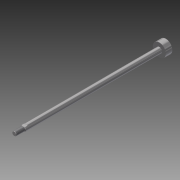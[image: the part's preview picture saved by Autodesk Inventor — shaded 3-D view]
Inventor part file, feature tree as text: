
AUTODESK INVENTOR PART (.ipt)
format: ipt  version: 2016 SP1 (Build 200210100, 210)  size: 106,496 bytes
history: native  units: in
note: dims shown in document units (in); Inventor stores cm internally (conversion verified against a paired STEP export)
features: other x7, sketch x3, extrude x2, revolve x1, thread x1
ambient origin geometry x8: Origin, YZ Plane, XZ Plane, XY Plane, X Axis, Y Axis, Z Axis, Center Point
bodies: Solid1 (feature_tree)
feature tree (14):
  revolve  "Revolution1"  [1 undecoded]
  thread  "Thread1"  [1 undecoded]
  extrude  "Extrusion1"  TaperAngle=0.0deg  [1 undecoded]
  extrude  "Extrusion2"  [1 undecoded]
  other  "conn_XY"
  other  "conn_YZ"
  other  "conn_ZX"
  other  "conn_X"
  other  "conn_Y"
  other  "conn_Z"
  other  "conn_Center"
  sketch  "Sketch_1"  dims[d0=360.0deg d1=0.4787in d2=0.0in d3=0.63in d4=0.0in]
  sketch  "Sketch_2"  dims[d5=0.63in d6=0.0in d7=0.0in]
  sketch  "Sketch_3"
note: 4 required parameter values undecoded (feature->parameter linkage not recoverable at this tier; creation-order binding heuristic only, values carry confidence <= 0.55)